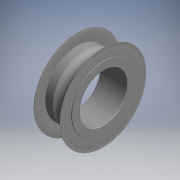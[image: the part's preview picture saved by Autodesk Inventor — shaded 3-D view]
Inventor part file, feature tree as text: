
AUTODESK INVENTOR PART (.ipt)
format: ipt  version: 2017.3 (Build 213256000, 256)  size: 196,096 bytes
history: native  units: mm (DEFAULTED — no unit token found)
features: revolve x3, sketch x3
ambient origin geometry x8: Origin, YZ Plane, XZ Plane, XY Plane, X Axis, Y Axis, Z Axis, Center Point
bodies: Solid1 (feature_tree)
feature tree (6):
  revolve  "Revolution1"  Angle=360.0deg
  revolve  "Revolution2"  [1 undecoded]
  revolve  "Revolution3"  [1 undecoded]
  sketch  "Sketch_17"  dims[d0=360.0deg d1=360.0deg]
  sketch  "Sketch_20"  dims[d2=360.0deg]
  sketch  "Sketch_21"
note: 2 required parameter values undecoded (feature->parameter linkage not recoverable at this tier; creation-order binding heuristic only, values carry confidence <= 0.55)
